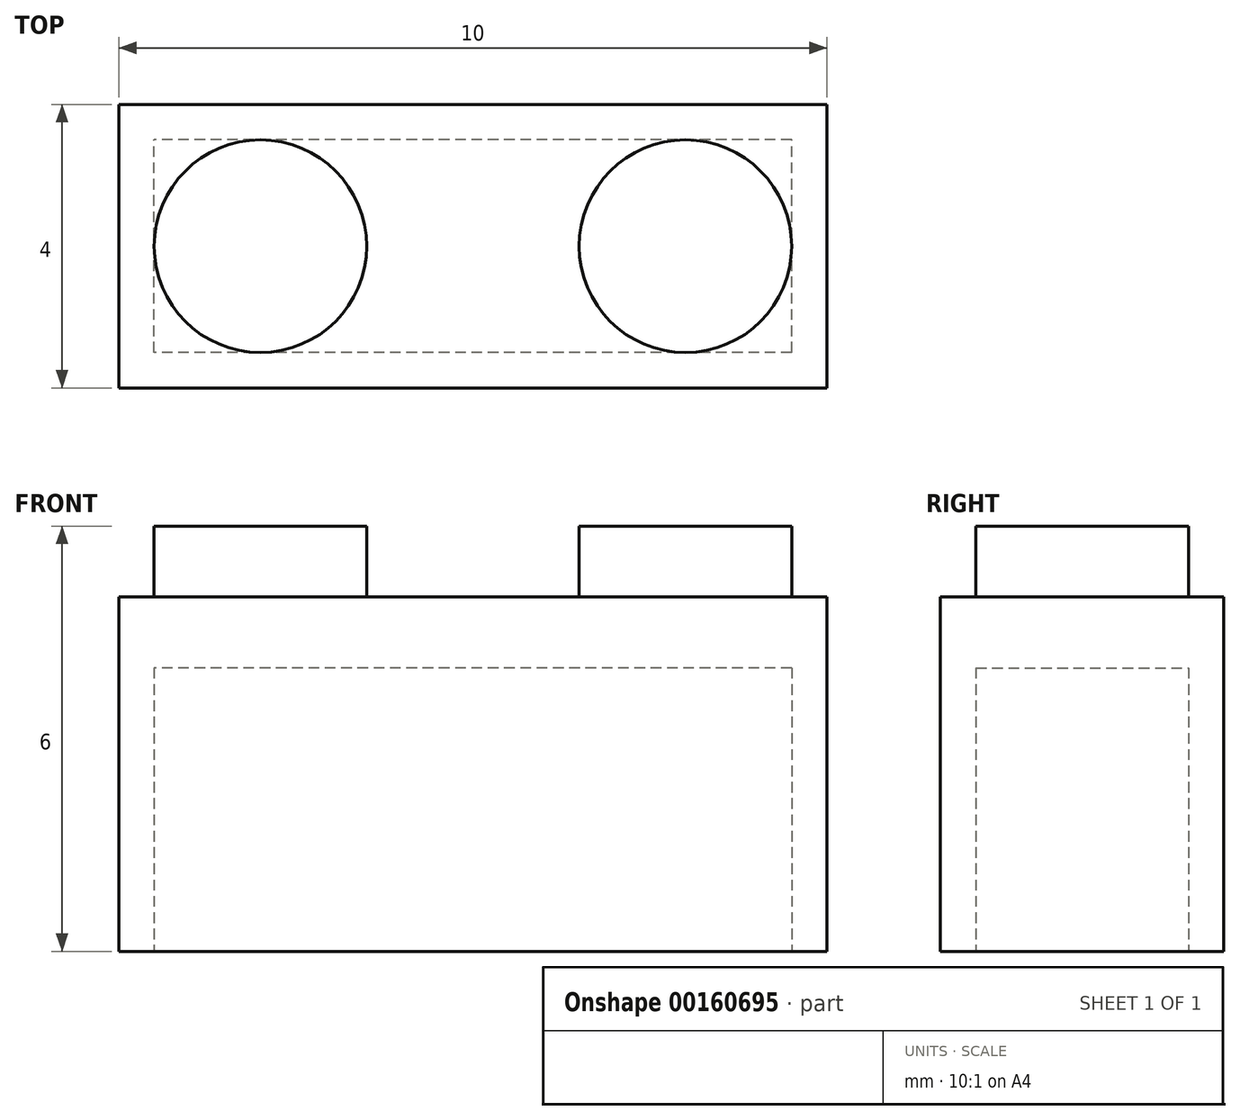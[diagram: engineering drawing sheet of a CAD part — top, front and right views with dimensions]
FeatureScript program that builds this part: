
annotation { "Feature Type Name" : "Feature", "Feature Type Description" : "" }
export const myFeature = defineFeature(function(context is Context, id is Id, definition is map)
    precondition{}
    {
        {
            var Q0;
            Q0=qCreatedBy(makeId("Top.planeOp"),FACE);
            var sketch = newSketch(context, id + "F0", { "sketchPlane" : qUnion([Q0])});
            skLineSegment(sketch, "E0.bottom", {"start": v(5, 2) * mm, "end": v(-5, 2) * mm});
            skLineSegment(sketch, "E0.top", {"start": v(5, -2) * mm, "end": v(-5, -2) * mm});
            skLineSegment(sketch, "E0.left", {"start": v(5, 2) * mm, "end": v(5, -2) * mm});
            skLineSegment(sketch, "E0.right", {"start": v(-5, 2) * mm, "end": v(-5, -2) * mm});
            skPoint(sketch, "E0.middle", {"position": v(0, 0) * mm});
            skSolve(sketch);
        }
        {
            var Q0;
            Q0 = qSketchRegion(id + "F0", true);
            extrude(context, id + "F1", {"entities" : qUnion([Q0]), "depth" : 5 * mm});
        }
        {
            var Q0;
            Q0=makeQuery(id+"F1.opExtrude","CAP_FACE",FACE,{"disambiguationData":[OSD([sQuery(id+"F0.wireOp",EDGE,"E0.bottom"),sQuery(id+"F0.wireOp",EDGE,"E0.top"),sQuery(id+"F0.wireOp",EDGE,"E0.left"),sQuery(id+"F0.wireOp",EDGE,"E0.right")])],"isStart":false});
            var sketch = newSketch(context, id + "F2", { "sketchPlane" : qUnion([Q0])});
            skCircle(sketch, "E1", {"center": v(-3, 0) * mm, "radius": 1.5 * mm});
            skCircle(sketch, "E2", {"center": v(3, 0) * mm, "radius": 1.5 * mm});
            skSolve(sketch);
        }
        {
            var Q0;
            Q0 = qSketchRegion(id + "F2", true);
            extrude(context, id + "F3", {"entities" : qUnion([Q0]), "operationType" : NewBodyOperationType.ADD, "depth" : 1 * mm});
        }
        {
            var Q0;
            Q0=makeQuery(id+"F1.opExtrude","CAP_FACE",FACE,{"disambiguationData":[OSD([sQuery(id+"F0.wireOp",EDGE,"E0.bottom"),sQuery(id+"F0.wireOp",EDGE,"E0.top"),sQuery(id+"F0.wireOp",EDGE,"E0.left"),sQuery(id+"F0.wireOp",EDGE,"E0.right")])],"isStart":true});
            var sketch = newSketch(context, id + "F4", { "sketchPlane" : qUnion([Q0])});
            skLineSegment(sketch, "E3.bottom", {"start": v(4.5, 1.5) * mm, "end": v(-4.5, 1.5) * mm});
            skLineSegment(sketch, "E3.top", {"start": v(4.5, -1.5) * mm, "end": v(-4.5, -1.5) * mm});
            skLineSegment(sketch, "E3.left", {"start": v(4.5, 1.5) * mm, "end": v(4.5, -1.5) * mm});
            skLineSegment(sketch, "E3.right", {"start": v(-4.5, 1.5) * mm, "end": v(-4.5, -1.5) * mm});
            skPoint(sketch, "E3.middle", {"position": v(0, 0) * mm});
            skSolve(sketch);
        }
        {
            var Q0;
            Q0 = qSketchRegion(id + "F4", true);
            extrude(context, id + "F5", {"entities" : qUnion([Q0]), "operationType" : NewBodyOperationType.REMOVE, "oppositeDirection" : true, "depth" : 4 * mm});
        }
    });
